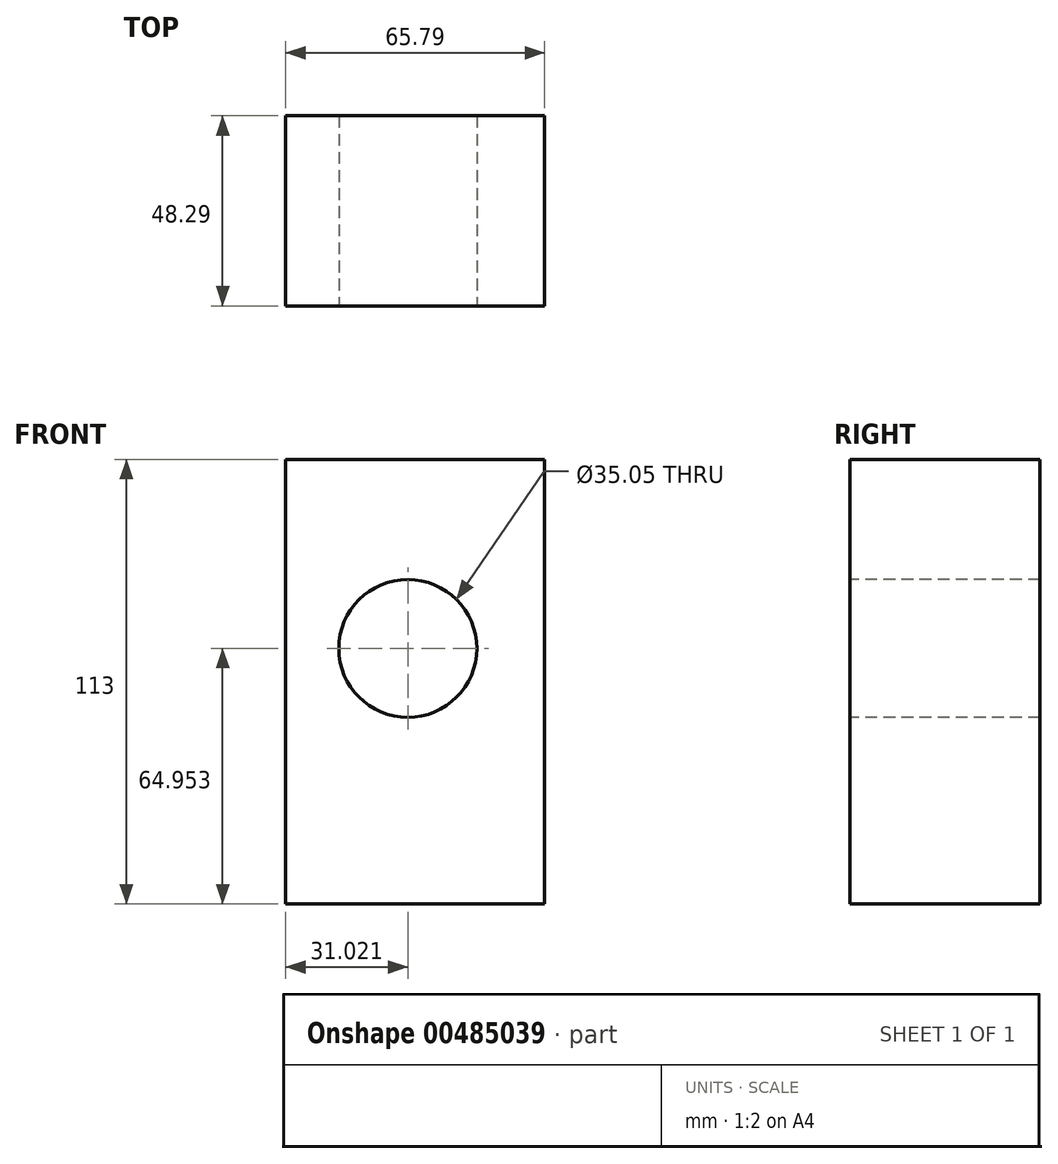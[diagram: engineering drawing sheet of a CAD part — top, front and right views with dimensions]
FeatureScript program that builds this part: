
annotation { "Feature Type Name" : "Feature", "Feature Type Description" : "" }
export const myFeature = defineFeature(function(context is Context, id is Id, definition is map)
    precondition{}
    {
        {
            var Q0;
            Q0=qCreatedBy(makeId("Top.planeOp"),FACE);
            var sketch = newSketch(context, id + "F0", { "sketchPlane" : qUnion([Q0])});
            skLineSegment(sketch, "E0.bottom", {"start": v(0, 0) * mm, "end": v(65.8, 0) * mm});
            skLineSegment(sketch, "E0.top", {"start": v(0, -48.29) * mm, "end": v(65.8, -48.29) * mm});
            skLineSegment(sketch, "E0.left", {"start": v(0, 0) * mm, "end": v(0, -48.29) * mm});
            skLineSegment(sketch, "E0.right", {"start": v(65.8, 0) * mm, "end": v(65.8, -48.29) * mm});
            skSolve(sketch);
        }
        {
            var Q0;
            Q0 = qSketchRegion(id + "F0", true);
            extrude(context, id + "F1", {"entities" : qUnion([Q0]), "depth" : 113 * mm, "offsetDistance" : 25 * mm});
        }
        {
            var Q0;
            Q0=makeQuery(id+"F1.opExtrude","SWEPT_FACE",FACE,{"disambiguationData":[OSD([sQuery(id+"F0.wireOp",EDGE,"E0.top")])]});
            var sketch = newSketch(context, id + "F2", { "sketchPlane" : qUnion([Q0])});
            skCircle(sketch, "E1", {"center": v(31.02, 64.95) * mm, "radius": 17.53 * mm});
            skSolve(sketch);
        }
        {
            var Q0;
            Q0 = qSketchRegion(id + "F2", true);
            extrude(context, id + "F3", {"entities" : qUnion([Q0]), "operationType" : NewBodyOperationType.REMOVE, "oppositeDirection" : true, "depth" : 190 * mm, "offsetDistance" : 25 * mm});
        }
    });
